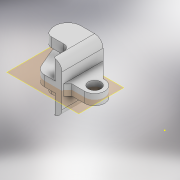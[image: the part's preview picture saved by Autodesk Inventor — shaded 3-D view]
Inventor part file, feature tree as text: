
AUTODESK INVENTOR PART (.ipt)
format: ipt  version: 2022 (Build 260153000, 153)  size: 240,128 bytes
history: native  units: mm
features: sketch x6, extrude x5, fillet x5, mirror x2, chamfer x2, projected_geometry x2, plane x1
ambient origin geometry x8: Origin, YZ Plane, XZ Plane, XY Plane, X Axis, Y Axis, Z Axis, Center Point
bodies: Solid1 (feature_tree)
feature tree (23):
  extrude  "Extrusion1"  Depth=9.5mm
  extrude  "Extrusion2"  Depth=10.4mm
  extrude  "Extrusion3"  Depth=4.0mm
  plane  "Work Plane1"
  mirror  "Mirror1"
  sketch  "Sketch6"  dims[d14=2.0mm d15=2.0mm d16=45.0deg d17=4.0mm]
  chamfer  "Chamfer1"  Distance=9.25mm
  fillet  "Fillet2"  Radius=4.5mm
  extrude  "Extrusion4"  Depth=4.0mm
  extrude  "Extrusion5"  Depth=1.0mm TaperAngle=0.0deg
  mirror  "Mirror2"
  fillet  "Fillet3"  Radius=11.983mm
  fillet  "Fillet4"  Radius=6.25mm
  fillet  "Fillet5"  Radius=13.5mm
  fillet  "Fillet6"  Radius=1.0mm
  chamfer  "Chamfer2"  Distance=11.5mm
  sketch  "Sketch2"  dims[d0=5.9mm d1=9.5mm]
  sketch  "Sketch4"  dims[d2=8.0mm d4=10.4mm]
  sketch  "Sketch5"  dims[d6=5.0mm d7=0.0mm d8=4.0mm d9=9.25mm d10=0.0mm d11=4.5mm d12=0.0mm]
  projected_geometry  "Projected Loop1"
  sketch  "Sketch7"  dims[d18=3.5mm d19=4.5mm d20=0.0mm d21=11.983mm d22=6.25mm d24=13.5mm d25=1.0mm]
  sketch  "Sketch8"  dims[d26=0.5mm d28=11.5mm d29=10.0mm d30=0.0mm d31=3.0mm d32=3.0mm d33=5.0mm d34=1.0mm d35=7.23mm d36=2.0mm d37=45.0deg]
  projected_geometry  "Projected Loop2"
